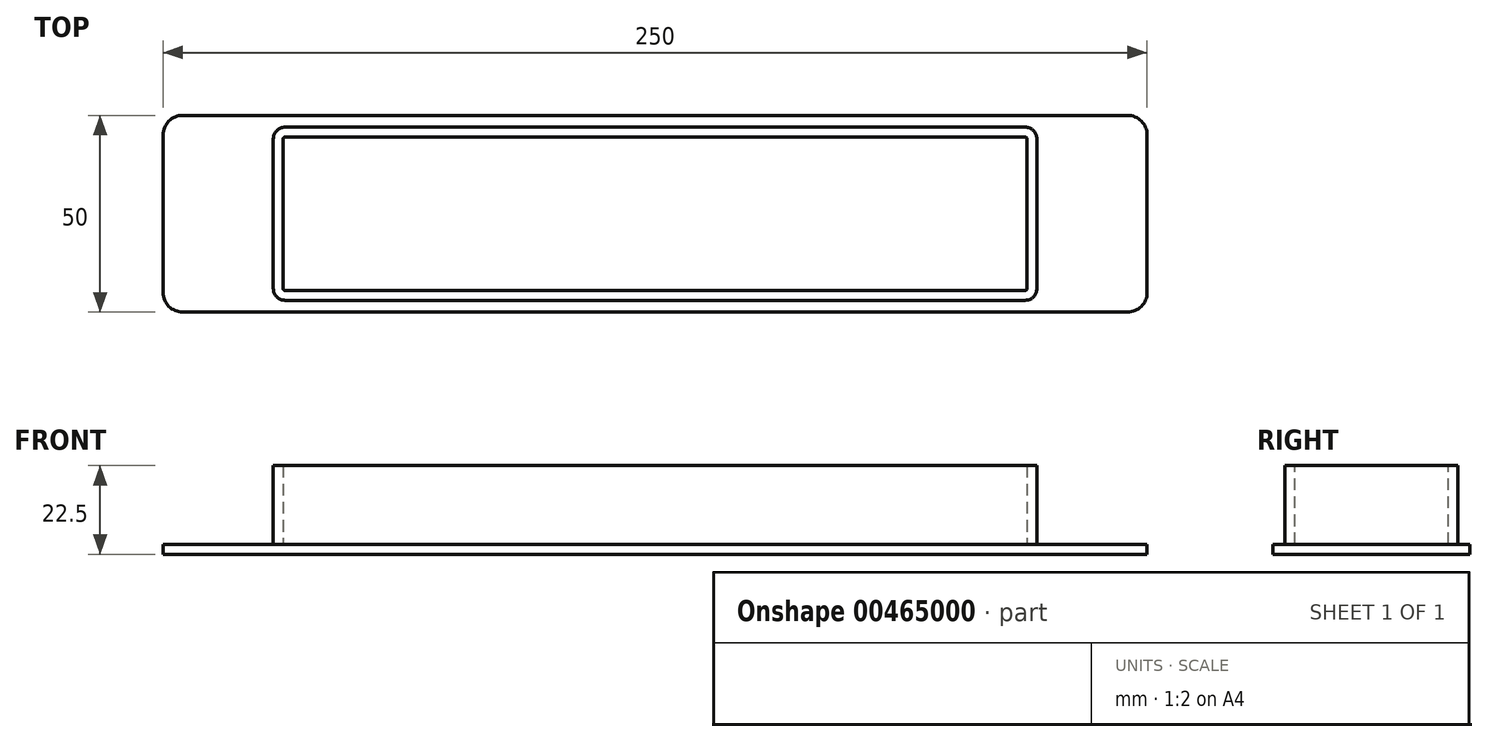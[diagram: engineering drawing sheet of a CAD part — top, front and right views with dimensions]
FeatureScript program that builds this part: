
annotation { "Feature Type Name" : "Feature", "Feature Type Description" : "" }
export const myFeature = defineFeature(function(context is Context, id is Id, definition is map)
    precondition{}
    {
        {
            var Q0;
            Q0=qCreatedBy(makeId("Top.planeOp"),FACE);
            var sketch = newSketch(context, id + "F0", { "sketchPlane" : qUnion([Q0])});
            skLineSegment(sketch, "E0.bottom", {"start": v(0, 0) * mm, "end": v(-200, 0) * mm, "construction": true});
            skLineSegment(sketch, "E0.top", {"start": v(0, 50) * mm, "end": v(-200, 50) * mm, "construction": true});
            skLineSegment(sketch, "E0.left", {"start": v(0, 0) * mm, "end": v(0, 50) * mm, "construction": true});
            skLineSegment(sketch, "E0.right", {"start": v(-200, 0) * mm, "end": v(-200, 50) * mm, "construction": true});
            skLineSegment(sketch, "E1.bottom", {"start": v(-225, 50) * mm, "end": v(25, 50) * mm});
            skLineSegment(sketch, "E1.top", {"start": v(-225, 0) * mm, "end": v(25, 0) * mm});
            skLineSegment(sketch, "E1.left", {"start": v(-225, 50) * mm, "end": v(-225, 0) * mm});
            skLineSegment(sketch, "E1.right", {"start": v(25, 50) * mm, "end": v(25, 0) * mm});
            skSolve(sketch);
        }
        {
            var Q0;
            Q0=qSketchRegion(id+"F0",true);
            extrude(context, id + "F1", {"entities" : qUnion([Q0]), "depth" : 2.5 * mm});
        }
        {
            var Q0;
            Q0=makeQuery(id+"F1.opExtrude","CAP_FACE",FACE,{"disambiguationData":[OSD([sQuery(id+"F0.wireOp",EDGE,"E1.bottom"),sQuery(id+"F0.wireOp",EDGE,"E1.top"),sQuery(id+"F0.wireOp",EDGE,"E1.left"),sQuery(id+"F0.wireOp",EDGE,"E1.right")])],"isStart":false});
            var sketch = newSketch(context, id + "F2", { "sketchPlane" : qUnion([Q0])});
            skLineSegment(sketch, "E2.bottom", {"start": v(-197, 47) * mm, "end": v(-3, 47) * mm});
            skLineSegment(sketch, "E2.top", {"start": v(-197, 3) * mm, "end": v(-3, 3) * mm});
            skLineSegment(sketch, "E2.left", {"start": v(-197, 47) * mm, "end": v(-197, 3) * mm});
            skLineSegment(sketch, "E2.right", {"start": v(-3, 47) * mm, "end": v(-3, 3) * mm});
            skSolve(sketch);
        }
        {
            var Q0;
            Q0 = qSketchRegion(id + "F2", true);
            extrude(context, id + "F3", {"entities" : qUnion([Q0]), "operationType" : NewBodyOperationType.ADD, "depth" : 20 * mm});
        }
        {
            var Q0;
            Q0=makeQuery(id+"F3.opExtrude","SWEPT_EDGE",EDGE,{"disambiguationData":[OSD([sQuery(id+"F2.wireOp",EDGE,"E2.top"),sQuery(id+"F2.wireOp",EDGE,"E2.left")])]});
            var Q1;
            Q1=makeQuery(id+"F3.opExtrude","SWEPT_EDGE",EDGE,{"disambiguationData":[OSD([sQuery(id+"F2.wireOp",EDGE,"E2.top"),sQuery(id+"F2.wireOp",EDGE,"E2.right")])]});
            var Q2;
            Q2=makeQuery(id+"F3.opExtrude","SWEPT_EDGE",EDGE,{"disambiguationData":[OSD([sQuery(id+"F2.wireOp",EDGE,"E2.bottom"),sQuery(id+"F2.wireOp",EDGE,"E2.right")])]});
            var Q3;
            Q3=makeQuery(id+"F3.opExtrude","SWEPT_EDGE",EDGE,{"disambiguationData":[OSD([sQuery(id+"F2.wireOp",EDGE,"E2.bottom"),sQuery(id+"F2.wireOp",EDGE,"E2.left")])]});
            fillet(context, id + "F4", {"entities" : qUnion([Q0, Q1, Q2, Q3]), "radius" : 3 * mm, "tangentPropagation" : true, "allowEdgeOverflow" : false});
        }
        {
            var Q0;
            Q0=makeQuery(id+"F3.opExtrude","CAP_FACE",FACE,{"disambiguationData":[OSD([sQuery(id+"F2.wireOp",EDGE,"E2.bottom"),sQuery(id+"F2.wireOp",EDGE,"E2.top"),sQuery(id+"F2.wireOp",EDGE,"E2.left"),sQuery(id+"F2.wireOp",EDGE,"E2.right")])],"isStart":false});
            shell(context, id + "F5", {"entities" : qUnion([Q0]), "thickness" : 2.5 * mm});
        }
        {
            var Q0;
            Q0=makeQuery(id+"F1.opExtrude","SWEPT_EDGE",EDGE,{"disambiguationData":[OSD([sQuery(id+"F0.wireOp",EDGE,"E1.top"),sQuery(id+"F0.wireOp",EDGE,"E1.right")])]});
            var Q1;
            Q1=makeQuery(id+"F1.opExtrude","SWEPT_EDGE",EDGE,{"disambiguationData":[OSD([sQuery(id+"F0.wireOp",EDGE,"E1.bottom"),sQuery(id+"F0.wireOp",EDGE,"E1.right")])]});
            var Q2;
            Q2=makeQuery(id+"F1.opExtrude","SWEPT_EDGE",EDGE,{"disambiguationData":[OSD([sQuery(id+"F0.wireOp",EDGE,"E1.bottom"),sQuery(id+"F0.wireOp",EDGE,"E1.left")])]});
            var Q3;
            Q3=makeQuery(id+"F1.opExtrude","SWEPT_EDGE",EDGE,{"disambiguationData":[OSD([sQuery(id+"F0.wireOp",EDGE,"E1.top"),sQuery(id+"F0.wireOp",EDGE,"E1.left")])]});
            fillet(context, id + "F6", {"entities" : qUnion([Q0, Q1, Q2, Q3]), "radius" : 5 * mm, "tangentPropagation" : true, "allowEdgeOverflow" : false});
        }
    });
